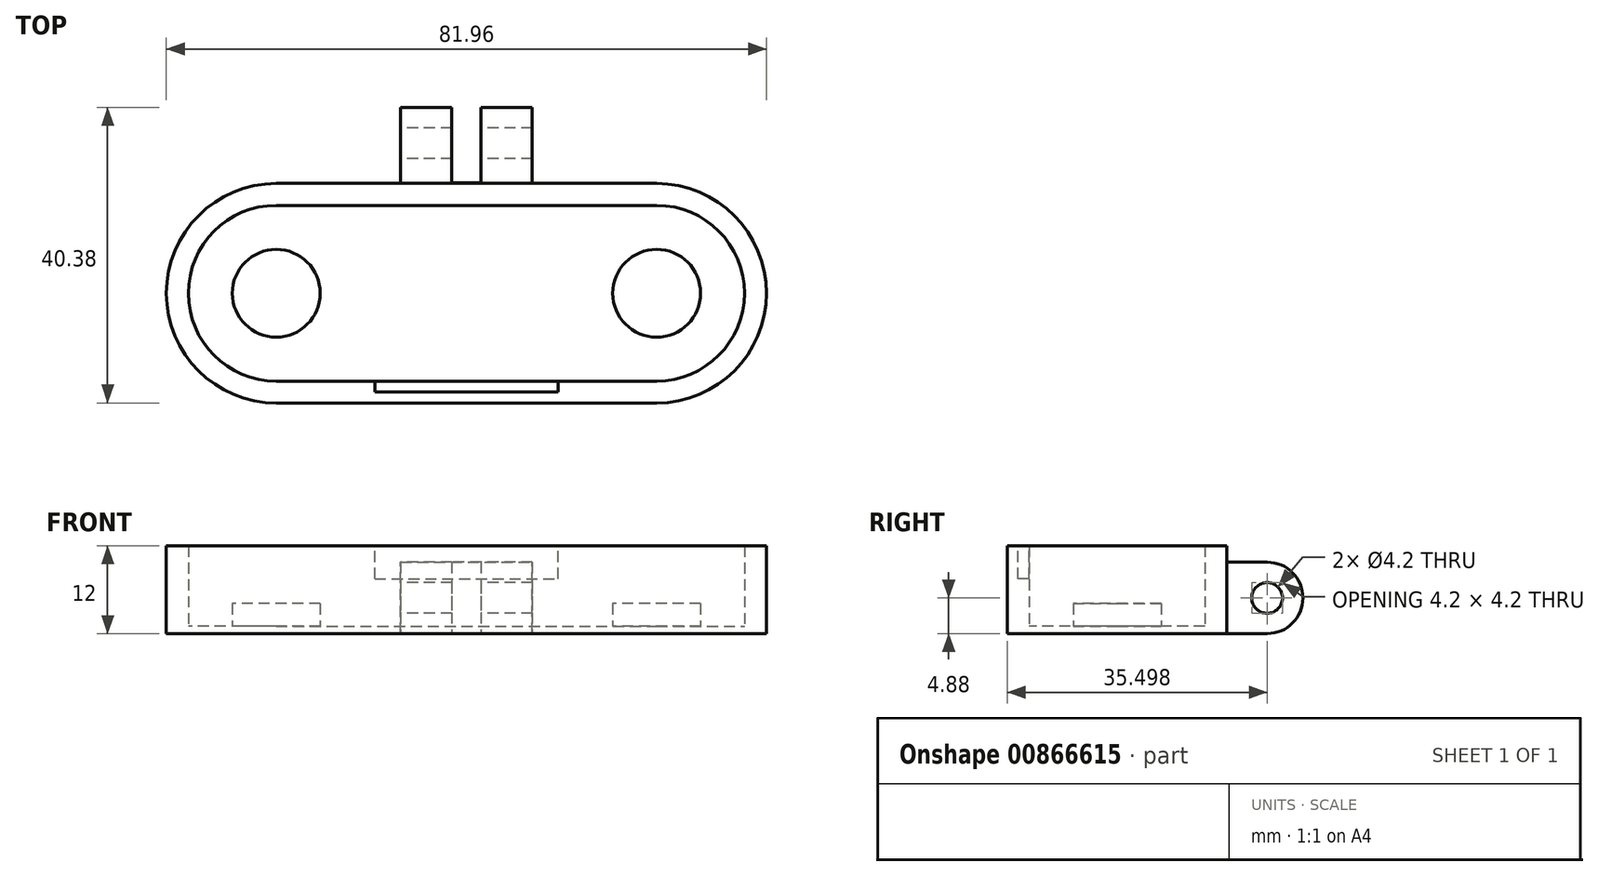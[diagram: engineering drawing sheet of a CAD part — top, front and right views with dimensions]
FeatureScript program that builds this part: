
annotation { "Feature Type Name" : "Feature", "Feature Type Description" : "" }
export const myFeature = defineFeature(function(context is Context, id is Id, definition is map)
    precondition{}
    {
        {
            var Q0;
            Q0=qCreatedBy(makeId("Top.planeOp"),FACE);
            var sketch = newSketch(context, id + "F0", { "sketchPlane" : qUnion([Q0])});
            skLineSegment(sketch, "E0.bottom", {"start": v(-25.97, 12) * mm, "end": v(25.97, 12) * mm});
            skLineSegment(sketch, "E0.top", {"start": v(-25.97, -12) * mm, "end": v(25.97, -12) * mm});
            skPoint(sketch, "E0.middle", {"position": v(0, 0) * mm});
            skArc(sketch, "E1", {"start": v(-25.97, 12) * mm, "mid": v(-37.98, 0) * mm, "end": v(-25.97, -12) * mm});
            skArc(sketch, "E2.MirrorC", {"start": v(25.97, 12) * mm, "mid": v(37.97, 0) * mm, "end": v(25.97, -12) * mm});
            skLineSegment(sketch, "E3.0", {"start": v(-25.97, 15) * mm, "end": v(25.97, 15) * mm});
            skArc(sketch, "E3.1", {"start": v(-25.98, 15) * mm, "mid": v(-40.97, 0) * mm, "end": v(-25.97, -15) * mm});
            skLineSegment(sketch, "E3.2", {"start": v(-25.97, -15) * mm, "end": v(25.97, -15) * mm});
            skArc(sketch, "E3.3", {"start": v(25.97, 15) * mm, "mid": v(40.97, 0) * mm, "end": v(25.97, -15) * mm});
            skCircle(sketch, "E4", {"center": v(-25.97, 0) * mm, "radius": 6 * mm});
            skCircle(sketch, "E5", {"center": v(25.97, 0) * mm, "radius": 6 * mm});
            skSolve(sketch);
        }
        {
            var Q0;
            Q0=makeQuery(id+"F0.imprint","IMPRINT",FACE,{"disambiguationData":[TD([[makeQuery(id+"F0.imprint","IMPRINT",EDGE,{"derivedFrom":sQuery(id+"F0.wireOp",EDGE,"E0.bottom")}),1.0]])]});
            extrude(context, id + "F1", {"entities" : qUnion([Q0]), "depth" : 12 * mm, "offsetDistance" : 25 * mm});
        }
        {
            var Q0;
            Q0=makeQuery(id+"F0.imprint","IMPRINT",FACE,{"disambiguationData":[TD([[makeQuery(id+"F0.imprint","IMPRINT",EDGE,{"derivedFrom":sQuery(id+"F0.wireOp",EDGE,"E0.bottom")}),-1.0]])]});
            extrude(context, id + "F2", {"entities" : qUnion([Q0]), "operationType" : NewBodyOperationType.ADD, "depth" : 1 * mm, "offsetDistance" : 25 * mm});
        }
        {
            var Q0;
            Q0=makeQuery(id+"F1.opExtrude","CAP_FACE",FACE,{"disambiguationData":[OSD([sQuery(id+"F0.wireOp",EDGE,"E0.bottom"),sQuery(id+"F0.wireOp",EDGE,"E0.top"),sQuery(id+"F0.wireOp",EDGE,"E1"),sQuery(id+"F0.wireOp",EDGE,"E2.MirrorC"),sQuery(id+"F0.wireOp",EDGE,"E3.0"),sQuery(id+"F0.wireOp",EDGE,"E3.1"),sQuery(id+"F0.wireOp",EDGE,"E3.2"),sQuery(id+"F0.wireOp",EDGE,"E3.3")])],"isStart":false});
            var sketch = newSketch(context, id + "F3", { "sketchPlane" : qUnion([Q0])});
            skLineSegment(sketch, "E6.bottom", {"start": v(-12.5, -11.5) * mm, "end": v(12.5, -11.5) * mm});
            skLineSegment(sketch, "E6.top", {"start": v(-12.5, -13.51) * mm, "end": v(12.5, -13.51) * mm});
            skLineSegment(sketch, "E6.left", {"start": v(-12.5, -11.5) * mm, "end": v(-12.5, -13.51) * mm});
            skLineSegment(sketch, "E6.right", {"start": v(12.5, -11.5) * mm, "end": v(12.5, -13.51) * mm});
            skPoint(sketch, "E6.middle", {"position": v(0, -12.5) * mm});
            skPoint(sketch, "E6.middle.positionSnap0", {"position": v(0, -12) * mm});
            skPoint(sketch, "E6.centerSnap0", {"position": v(0, -12) * mm});
            skSolve(sketch);
        }
        {
            var Q0;
            Q0 = qSketchRegion(id + "F3", true);
            extrude(context, id + "F4", {"entities" : qUnion([Q0]), "operationType" : NewBodyOperationType.REMOVE, "oppositeDirection" : true, "depth" : 4.5 * mm, "offsetDistance" : 25 * mm});
        }
        {
            var Q0;
            Q0=makeQuery(id+"F0.imprint","IMPRINT",FACE,{"disambiguationData":[TD([[makeQuery(id+"F0.imprint","IMPRINT",EDGE,{"derivedFrom":sQuery(id+"F0.wireOp",EDGE,"E4")}),1.0]])]});
            var Q1;
            Q1=makeQuery(id+"F0.imprint","IMPRINT",FACE,{"disambiguationData":[TD([[makeQuery(id+"F0.imprint","IMPRINT",EDGE,{"derivedFrom":sQuery(id+"F0.wireOp",EDGE,"E5")}),1.0]])]});
            extrude(context, id + "F5", {"entities" : qUnion([Q0, Q1]), "operationType" : NewBodyOperationType.ADD, "depth" : 4.1 * mm, "offsetDistance" : 25 * mm});
        }
        {
            var Q0;
            Q0=qCreatedBy(makeId("Right.planeOp"),FACE);
            var sketch = newSketch(context, id + "F6", { "sketchPlane" : qUnion([Q0])});
            skLineSegment(sketch, "E7.bottom", {"start": v(12.97, 0) * mm, "end": v(20.5, 0) * mm});
            skLineSegment(sketch, "E7.top", {"start": v(12.97, 9.76) * mm, "end": v(20.5, 9.76) * mm});
            skLineSegment(sketch, "E7.left", {"start": v(12.97, 0) * mm, "end": v(12.97, 9.76) * mm});
            skArc(sketch, "E8", {"start": v(20.5, 0) * mm, "mid": v(25.38, 4.88) * mm, "end": v(20.5, 9.76) * mm});
            skCircle(sketch, "E9", {"center": v(20.5, 4.88) * mm, "radius": 2.1 * mm});
            skSolve(sketch);
        }
        {
            var Q0;
            Q0=makeQuery(id+"F6.imprint","IMPRINT",FACE,{"disambiguationData":[TD([[makeQuery(id+"F6.imprint","IMPRINT",EDGE,{"derivedFrom":sQuery(id+"F6.wireOp",EDGE,"E7.bottom")}),1.0]])]});
            extrude(context, id + "F7", {"entities" : qUnion([Q0]), "operationType" : NewBodyOperationType.ADD, "endBound" : BoundingType.SYMMETRIC, "depth" : 18 * mm, "offsetDistance" : 25 * mm});
        }
        {
            var Q0;
            Q0=qCreatedBy(makeId("Top.planeOp"),FACE);
            var sketch = newSketch(context, id + "F8", { "sketchPlane" : qUnion([Q0])});
            skLineSegment(sketch, "E10.bottom", {"start": v(-2, 15.08) * mm, "end": v(2, 15.08) * mm});
            skLineSegment(sketch, "E10.top", {"start": v(-2, 30.08) * mm, "end": v(2, 30.08) * mm});
            skLineSegment(sketch, "E10.left", {"start": v(-2, 15.08) * mm, "end": v(-2, 30.08) * mm});
            skLineSegment(sketch, "E10.right", {"start": v(2, 15.08) * mm, "end": v(2, 30.08) * mm});
            skSolve(sketch);
        }
        {
            var Q0;
            Q0=makeQuery(id+"F8.imprint","IMPRINT",FACE,{"disambiguationData":[TD([[makeQuery(id+"F8.imprint","IMPRINT",EDGE,{"derivedFrom":sQuery(id+"F8.wireOp",EDGE,"E10.bottom")}),1.0]])]});
            extrude(context, id + "F9", {"entities" : qUnion([Q0]), "operationType" : NewBodyOperationType.REMOVE, "endBound" : BoundingType.SYMMETRIC, "depth" : 30 * mm, "offsetDistance" : 25 * mm});
        }
    });
